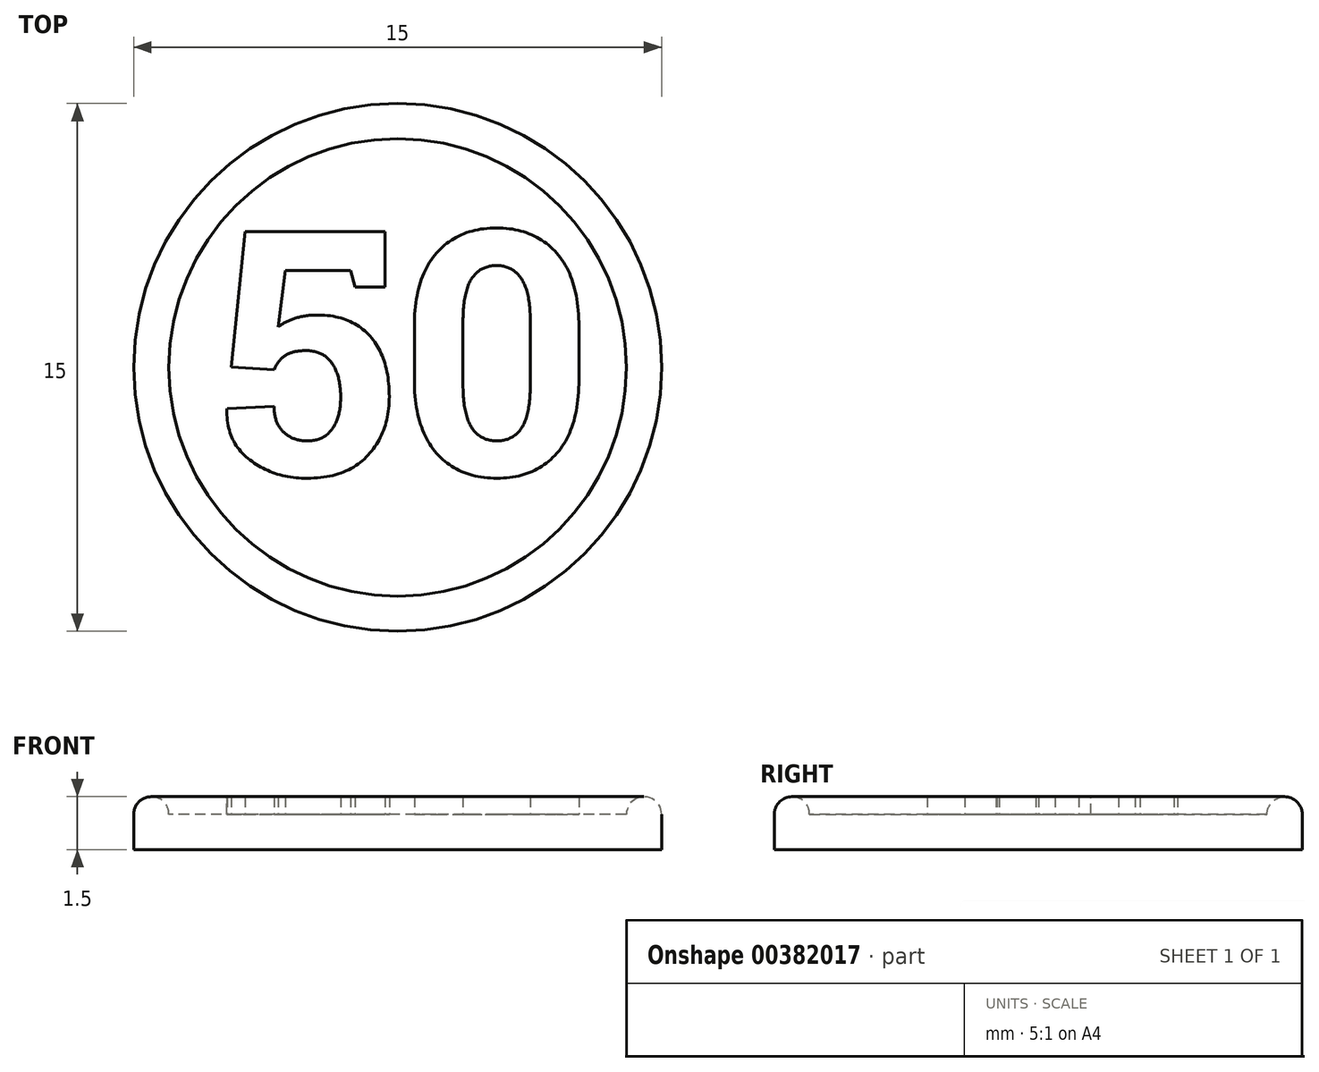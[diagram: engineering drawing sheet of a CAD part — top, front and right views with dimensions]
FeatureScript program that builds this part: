
annotation { "Feature Type Name" : "Feature", "Feature Type Description" : "" }
export const myFeature = defineFeature(function(context is Context, id is Id, definition is map)
    precondition{}
    {
        {
            var Q0;
            Q0=qCreatedBy(makeId("Top.planeOp"),FACE);
            var sketch = newSketch(context, id + "F0", { "sketchPlane" : qUnion([Q0])});
            skCircle(sketch, "E0", {"center": v(0, 0) * mm, "radius": 7.5 * mm});
            skCircle(sketch, "E1", {"center": v(0, 0) * mm, "radius": 6.5 * mm});
            skSolve(sketch);
        }
        {
            var Q0;
            Q0=makeQuery(id+"F0.imprint","IMPRINT",FACE,{"disambiguationData":[TD([[makeQuery(id+"F0.imprint","IMPRINT",EDGE,{"derivedFrom":sQuery(id+"F0.wireOp",EDGE,"E0")}),1.0]])]});
            extrude(context, id + "F1", {"entities" : qUnion([Q0]), "depth" : 1.5 * mm});
        }
        {
            var Q0;
            Q0=makeQuery(id+"F0.imprint","IMPRINT",FACE,{"disambiguationData":[TD([[makeQuery(id+"F0.imprint","IMPRINT",EDGE,{"derivedFrom":sQuery(id+"F0.wireOp",EDGE,"E1")}),1.0]])]});
            extrude(context, id + "F2", {"entities" : qUnion([Q0]), "operationType" : NewBodyOperationType.ADD, "depth" : 1 * mm});
        }
        {
            var Q0;
            Q0=makeQuery(id+"F1.opExtrude","CAP_EDGE",EDGE,{"disambiguationData":[OSD([sQuery(id+"F0.wireOp",EDGE,"E0")])],"isStart":false});
            fillet(context, id + "F3", {"entities" : qUnion([Q0]), "radius" : 0.5 * mm, "tangentPropagation" : true, "allowEdgeOverflow" : false});
        }
        {
            var Q0;
            Q0=makeQuery(id+"F1.opExtrude","CAP_EDGE",EDGE,{"disambiguationData":[OSD([sQuery(id+"F0.wireOp",EDGE,"E1")])],"isStart":false});
            fillet(context, id + "F4", {"entities" : qUnion([Q0]), "radius" : 0.5 * mm, "tangentPropagation" : true, "allowEdgeOverflow" : false});
        }
        {
            var Q0;
            Q0=makeQuery(id+"F2.opExtrude","CAP_FACE",FACE,{"disambiguationData":[OSD([sQuery(id+"F0.wireOp",EDGE,"E1")])],"isStart":false});
            var sketch = newSketch(context, id + "F5", { "sketchPlane" : qUnion([Q0])});
            skText(sketch, "E2", { "text": "50", "fontName": "RobotoSlab-Bold.ttf"});
            const initialGuessF5  = {"E2": [-0.00517, -0.00305, 1, 0, 0.007]};
            skSetInitialGuess(sketch, initialGuessF5);
            skSolve(sketch);
        }
        {
            var Q0;
            Q0=qSketchRegion(id+"F5",true);
            extrude(context, id + "F6", {"entities" : qUnion([Q0]), "operationType" : NewBodyOperationType.ADD, "depth" : 0.5 * mm});
        }
    });
